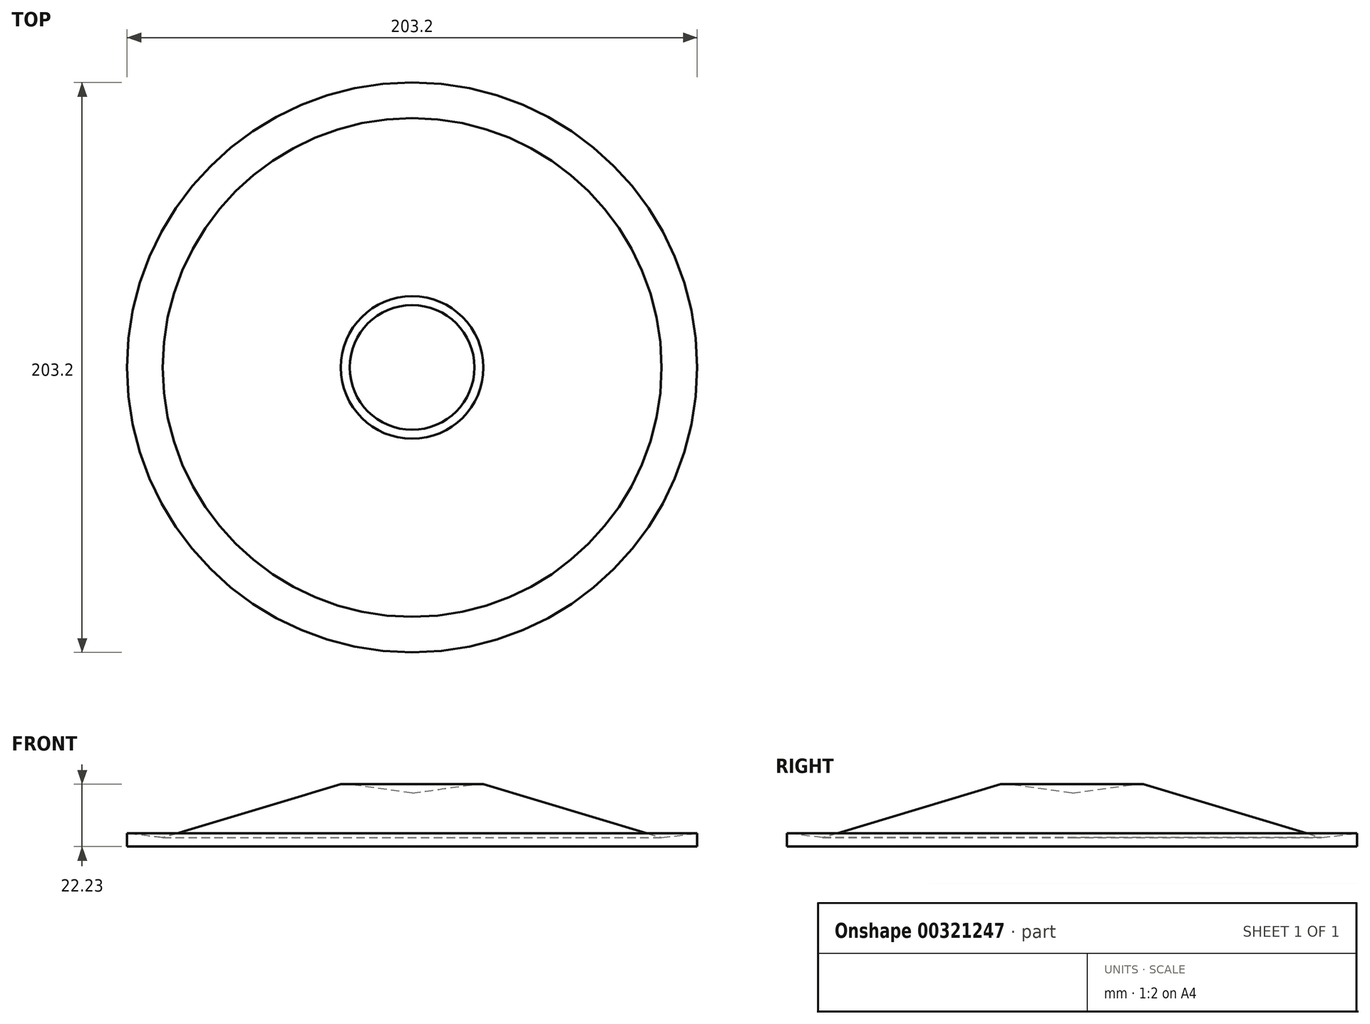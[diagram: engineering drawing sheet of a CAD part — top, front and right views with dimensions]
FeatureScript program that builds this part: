
annotation { "Feature Type Name" : "Feature", "Feature Type Description" : "" }
export const myFeature = defineFeature(function(context is Context, id is Id, definition is map)
    precondition{}
    {
        {
            var Q0;
            Q0=qCreatedBy(makeId("Front.planeOp"),FACE);
            var sketch = newSketch(context, id + "F0", { "sketchPlane" : qUnion([Q0])});
            skLineSegment(sketch, "E0", {"start": v(0, 19.05) * mm, "end": v(-22.23, 22.23) * mm});
            skLineSegment(sketch, "E1", {"start": v(-22.23, 22.23) * mm, "end": v(-25.4, 22.23) * mm});
            skLineSegment(sketch, "E2", {"start": v(-25.4, 22.23) * mm, "end": v(-88.9, 3.18) * mm});
            skLineSegment(sketch, "E3", {"start": v(-88.9, 3.18) * mm, "end": v(-101.6, 4.75) * mm});
            skLineSegment(sketch, "E4", {"start": v(-101.6, 4.75) * mm, "end": v(-101.6, 0) * mm});
            skLineSegment(sketch, "E5", {"start": v(-101.6, 0) * mm, "end": v(0, 0) * mm});
            skLineSegment(sketch, "E6", {"start": v(0, 0) * mm, "end": v(0, 19.05) * mm});
            skSolve(sketch);
        }
        {
            var Q0;
            Q0=makeQuery(id+"F0.imprint","IMPRINT",FACE,{"disambiguationData":[TD([[makeQuery(id+"F0.imprint","IMPRINT",EDGE,{"derivedFrom":sQuery(id+"F0.wireOp",EDGE,"E0")}),1.0]])]});
            var Q1;
            Q1=sQuery(id+"F0.wireOp",EDGE,"E6");
            revolve(context, id + "F1", {"entities" : qUnion([Q0]), "axis" : qUnion([Q1]), "revolveType" : RevolveType.FULL});
        }
    });
